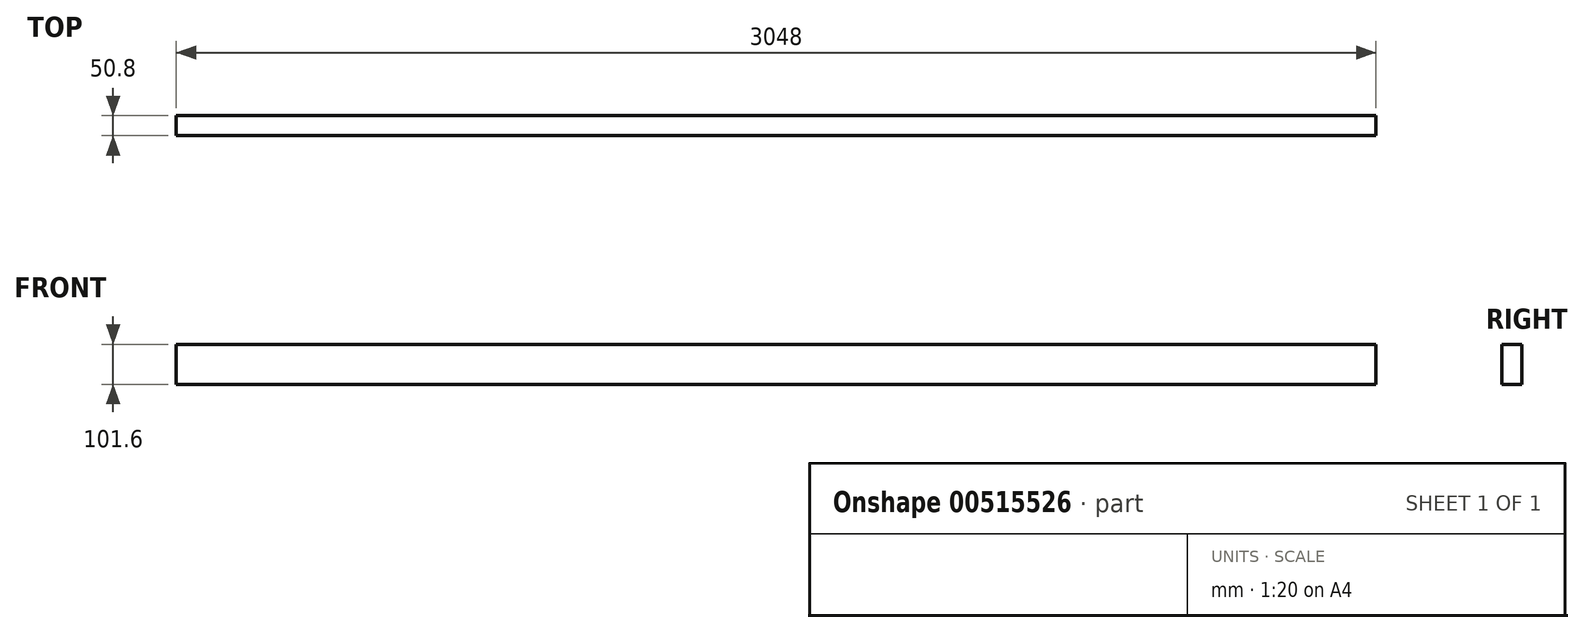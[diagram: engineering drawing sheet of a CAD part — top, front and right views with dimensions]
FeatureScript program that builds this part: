
annotation { "Feature Type Name" : "Feature", "Feature Type Description" : "" }
export const myFeature = defineFeature(function(context is Context, id is Id, definition is map)
    precondition{}
    {
        {
            var Q0;
            Q0=qCreatedBy(makeId("Right.planeOp"),FACE);
            var sketch = newSketch(context, id + "F0", { "sketchPlane" : qUnion([Q0])});
            skLineSegment(sketch, "E0", {"start": v(-25.4, -50.8) * mm, "end": v(-25.4, 50.8) * mm});
            skLineSegment(sketch, "E1", {"start": v(-25.4, 50.8) * mm, "end": v(25.4, 50.8) * mm});
            skLineSegment(sketch, "E2", {"start": v(25.4, 50.8) * mm, "end": v(25.4, -50.8) * mm});
            skLineSegment(sketch, "E3", {"start": v(25.4, -50.8) * mm, "end": v(-25.4, -50.8) * mm});
            skSolve(sketch);
        }
        {
            var Q0;
            Q0=makeQuery(id+"F0.imprint","IMPRINT",FACE,{"disambiguationData":[TD([[makeQuery(id+"F0.imprint","IMPRINT",EDGE,{"derivedFrom":sQuery(id+"F0.wireOp",EDGE,"E0")}),-1.0]])]});
            extrude(context, id + "F1", {"entities" : qUnion([Q0]), "depth" : 3048 * mm, "offsetDistance" : 25.4 * mm});
        }
    });
